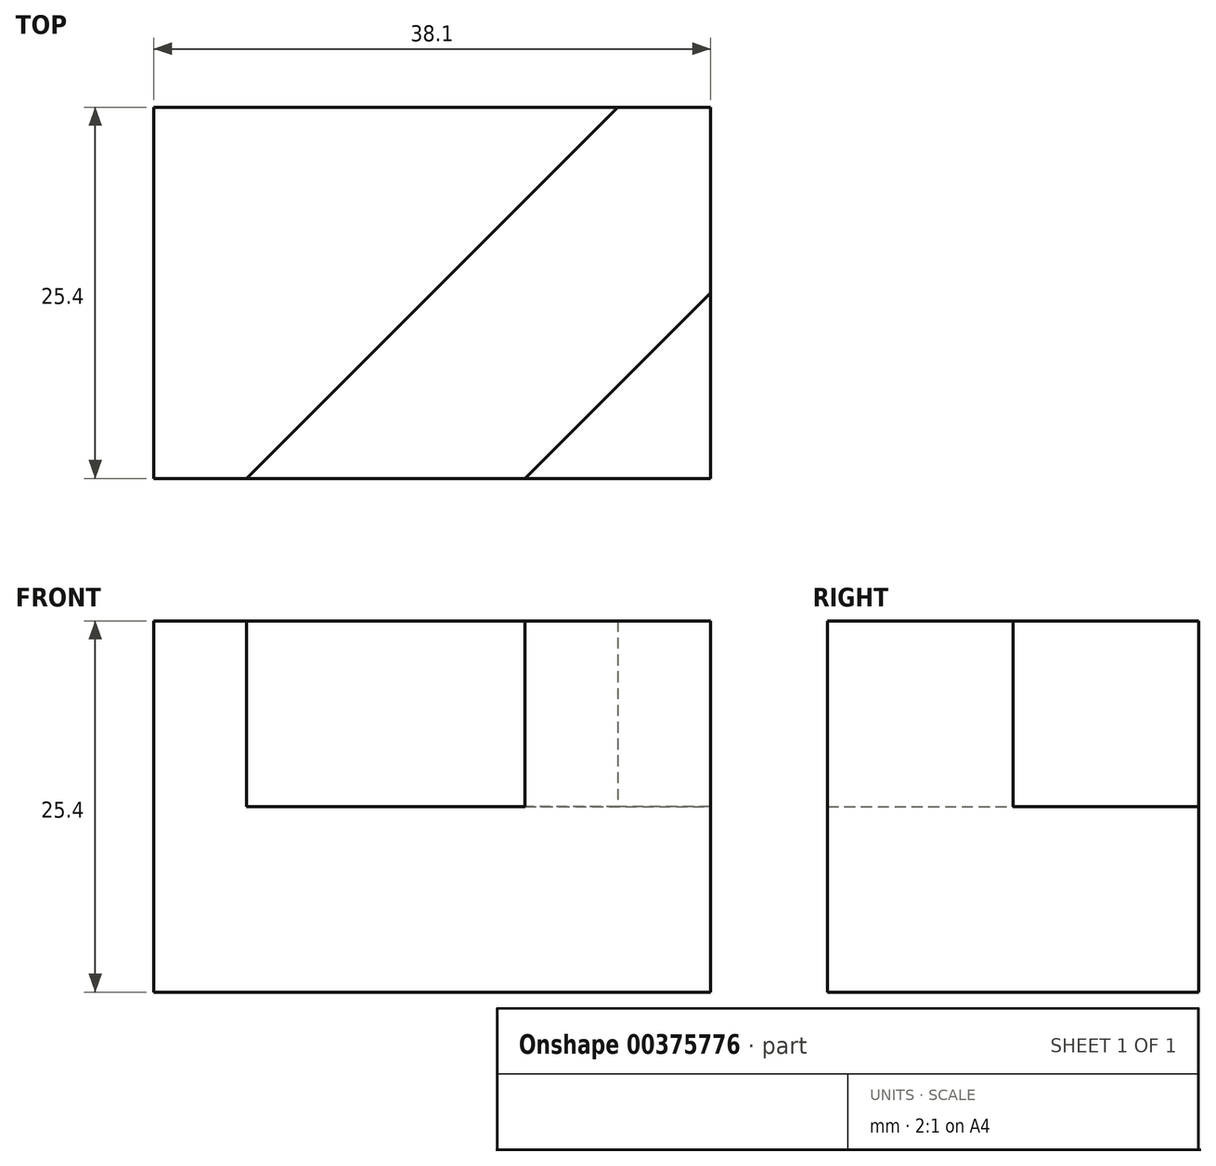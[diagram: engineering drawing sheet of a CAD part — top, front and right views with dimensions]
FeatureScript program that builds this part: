
annotation { "Feature Type Name" : "Feature", "Feature Type Description" : "" }
export const myFeature = defineFeature(function(context is Context, id is Id, definition is map)
    precondition{}
    {
        {
            var Q0;
            Q0=qCreatedBy(makeId("Front.planeOp"),FACE);
            var sketch = newSketch(context, id + "F0", { "sketchPlane" : qUnion([Q0])});
            skLineSegment(sketch, "E0", {"start": v(0, 0) * mm, "end": v(38.1, 0) * mm});
            skLineSegment(sketch, "E1", {"start": v(38.1, 0) * mm, "end": v(38.1, 12.7) * mm});
            skLineSegment(sketch, "E2", {"start": v(38.1, 12.7) * mm, "end": v(0, 12.7) * mm});
            skLineSegment(sketch, "E3", {"start": v(0, 12.7) * mm, "end": v(0, 0) * mm});
            skSolve(sketch);
        }
        {
            var Q0;
            Q0 = qSketchRegion(id + "F0", true);
            extrude(context, id + "F1", {"entities" : qUnion([Q0]), "depth" : 25.4 * mm});
        }
        {
            var Q0;
            Q0=makeQuery(id+"F1.opExtrude","SWEPT_FACE",FACE,{"disambiguationData":[OSD([sQuery(id+"F0.wireOp",EDGE,"E2")])]});
            var sketch = newSketch(context, id + "F2", { "sketchPlane" : qUnion([Q0])});
            skLineSegment(sketch, "E4", {"start": v(31.75, 0) * mm, "end": v(6.35, -25.4) * mm});
            skLineSegment(sketch, "E5", {"start": v(25.4, -25.4) * mm, "end": v(38.1, -12.7) * mm});
            skSolve(sketch);
        }
        {
            var Q0;
            {var subQ0=sQuery(id+"F2.wireOp",EDGE,"E4");Q0=makeQuery(id+"F2.imprint","IMPRINT",FACE,{"disambiguationData":[TD([[makeQuery(id+"F2.imprint","IMPRINT",EDGE,{"derivedFrom":subQ0}),-1.0]])]});}
            var Q1;
            {var subQ0=sQuery(id+"F2.wireOp",EDGE,"E5");Q1=makeQuery(id+"F2.imprint","IMPRINT",FACE,{"disambiguationData":[TD([[makeQuery(id+"F2.imprint","IMPRINT",EDGE,{"derivedFrom":subQ0}),-1.0]])]});}
            extrude(context, id + "F3", {"entities" : qUnion([Q0, Q1]), "operationType" : NewBodyOperationType.ADD, "depth" : 12.7 * mm});
        }
    });
